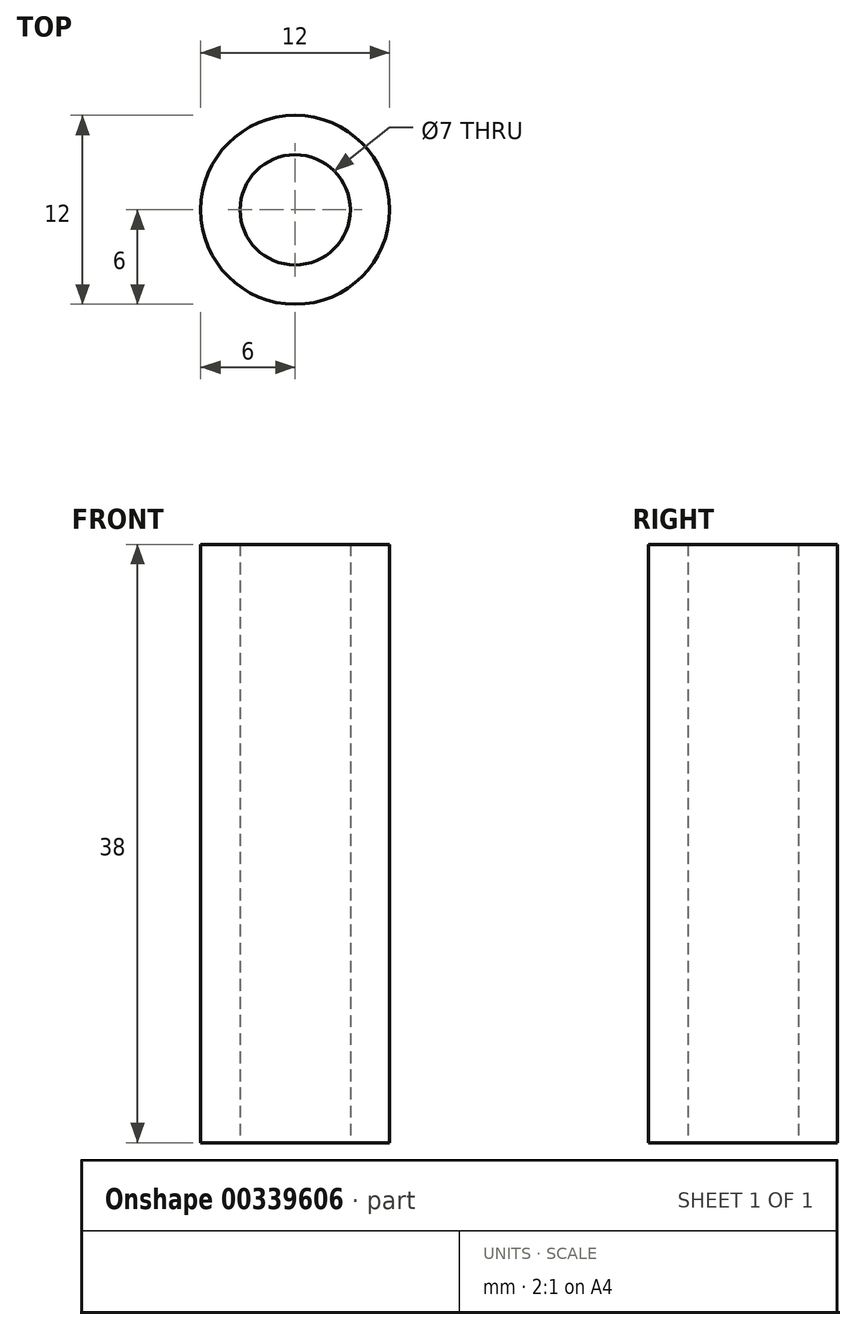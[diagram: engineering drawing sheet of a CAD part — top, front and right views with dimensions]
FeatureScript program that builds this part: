
annotation { "Feature Type Name" : "Feature", "Feature Type Description" : "" }
export const myFeature = defineFeature(function(context is Context, id is Id, definition is map)
    precondition{}
    {
        {
            var Q0;
            Q0=qCreatedBy(makeId("Top.planeOp"),FACE);
            var sketch = newSketch(context, id + "F0", { "sketchPlane" : qUnion([Q0])});
            skCircle(sketch, "E0", {"center": v(0, 0) * mm, "radius": 3.5 * mm});
            skCircle(sketch, "E1", {"center": v(0, 0) * mm, "radius": 6 * mm});
            skSolve(sketch);
        }
        {
            var Q0;
            Q0=qSketchRegion(id+"F0",true);
            extrude(context, id + "F1", {"entities" : qUnion([Q0]), "depth" : 38 * mm});
        }
    });
